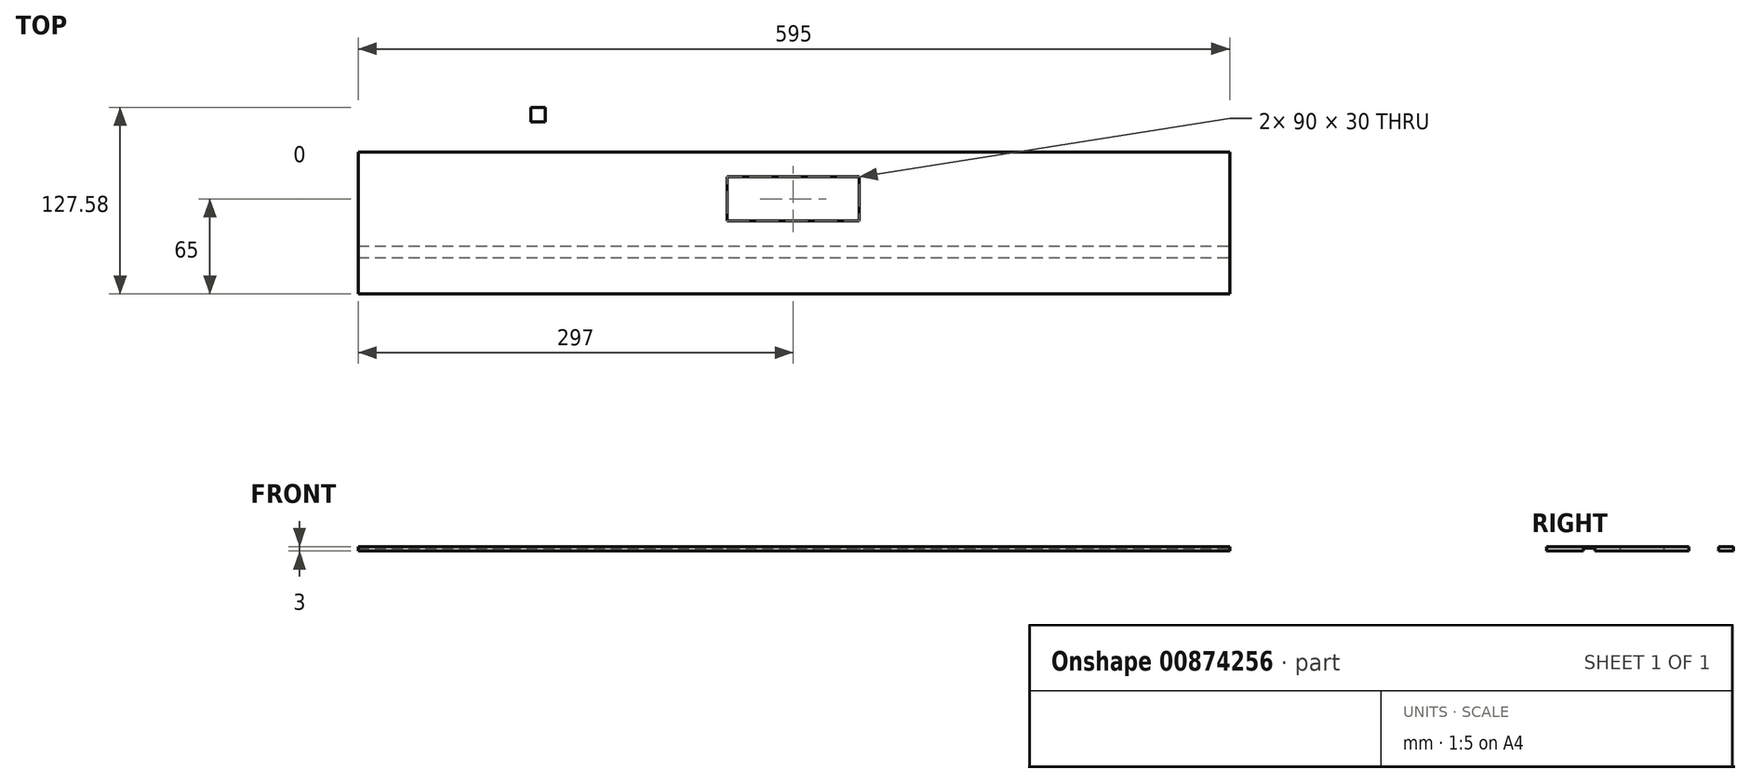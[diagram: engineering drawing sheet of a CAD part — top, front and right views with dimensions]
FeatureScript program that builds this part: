
annotation { "Feature Type Name" : "Feature", "Feature Type Description" : "" }
export const myFeature = defineFeature(function(context is Context, id is Id, definition is map)
    precondition{}
    {
        {
            var Q0;
            Q0=qCreatedBy(makeId("Top.planeOp"),FACE);
            var sketch = newSketch(context, id + "F0", { "sketchPlane" : qUnion([Q0])});
            skLineSegment(sketch, "E0.bottom", {"start": v(-297.5, 48.5) * mm, "end": v(297.5, 48.5) * mm});
            skLineSegment(sketch, "E0.top", {"start": v(-297.5, -48.5) * mm, "end": v(297.5, -48.5) * mm});
            skLineSegment(sketch, "E0.left", {"start": v(-297.5, 48.5) * mm, "end": v(-297.5, -48.5) * mm});
            skLineSegment(sketch, "E0.right", {"start": v(297.5, 48.5) * mm, "end": v(297.5, -48.5) * mm});
            skPoint(sketch, "E0.middle", {"position": v(0, 0) * mm});
            skLineSegment(sketch, "E1.bottom", {"start": v(-297.5, -23.5) * mm, "end": v(297.5, -23.5) * mm});
            skLineSegment(sketch, "E1.top", {"start": v(-297.5, -15.5) * mm, "end": v(297.5, -15.5) * mm});
            skLineSegment(sketch, "E1.left", {"start": v(-297.5, -23.5) * mm, "end": v(-297.5, -15.5) * mm});
            skLineSegment(sketch, "E1.right", {"start": v(297.5, -23.5) * mm, "end": v(297.5, -15.5) * mm});
            skLineSegment(sketch, "E2.bottom", {"start": v(-45.5, 31.5) * mm, "end": v(44.5, 31.5) * mm});
            skLineSegment(sketch, "E2.top", {"start": v(-45.5, 1.5) * mm, "end": v(44.5, 1.5) * mm});
            skLineSegment(sketch, "E2.left", {"start": v(-45.5, 31.5) * mm, "end": v(-45.5, 1.5) * mm});
            skLineSegment(sketch, "E2.right", {"start": v(44.5, 31.5) * mm, "end": v(44.5, 1.5) * mm});
            skLineSegment(sketch, "E3.bottom", {"start": v(-179.66, 79.08) * mm, "end": v(-169.66, 79.08) * mm});
            skLineSegment(sketch, "E3.top", {"start": v(-179.66, 69.08) * mm, "end": v(-169.66, 69.08) * mm});
            skLineSegment(sketch, "E3.left", {"start": v(-179.66, 79.08) * mm, "end": v(-179.66, 69.08) * mm});
            skLineSegment(sketch, "E3.right", {"start": v(-169.66, 79.08) * mm, "end": v(-169.66, 69.08) * mm});
            skSolve(sketch);
        }
        {
            var Q0;
            {var subQ2=sQuery(id+"F0.wireOp",EDGE,"E0.bottom");Q0=makeQuery(id+"F0.imprint","IMPRINT",FACE,{"disambiguationData":[TD([[makeQuery(id+"F0.imprint","IMPRINT",EDGE,{"derivedFrom":subQ2}),-1.0]])]});}
            var Q1;
            {var subQ0=sQuery(id+"F0.wireOp",EDGE,"E0.top");Q1=makeQuery(id+"F0.imprint","IMPRINT",FACE,{"disambiguationData":[TD([[makeQuery(id+"F0.imprint","IMPRINT",EDGE,{"derivedFrom":subQ0}),1.0]])]});}
            var Q2;
            {var subQ0=sQuery(id+"F0.wireOp",EDGE,"E1.bottom");Q2=makeQuery(id+"F0.imprint","IMPRINT",FACE,{"disambiguationData":[TD([[makeQuery(id+"F0.imprint","IMPRINT",EDGE,{"derivedFrom":subQ0}),1.0]])]});}
            extrude(context, id + "F1", {"entities" : qUnion([Q0, Q1, Q2]), "depth" : 3 * mm, "offsetDistance" : 25 * mm});
        }
        {
            var Q0;
            {var subQ0=sQuery(id+"F0.wireOp",EDGE,"E1.bottom");Q0=makeQuery(id+"F0.imprint","IMPRINT",FACE,{"disambiguationData":[TD([[makeQuery(id+"F0.imprint","IMPRINT",EDGE,{"derivedFrom":subQ0}),1.0]])]});}
            extrude(context, id + "F2", {"entities" : qUnion([Q0]), "operationType" : NewBodyOperationType.REMOVE, "depth" : 2 * mm, "offsetDistance" : 25 * mm});
        }
        {
            var Q0;
            Q0=makeQuery(id+"F0.imprint","IMPRINT",FACE,{"disambiguationData":[TD([[makeQuery(id+"F0.imprint","IMPRINT",EDGE,{"derivedFrom":sQuery(id+"F0.wireOp",EDGE,"E3.bottom")}),-1.0]])]});
            extrude(context, id + "F3", {"entities" : qUnion([Q0]), "depth" : 3 * mm, "offsetDistance" : 25 * mm});
        }
    });
